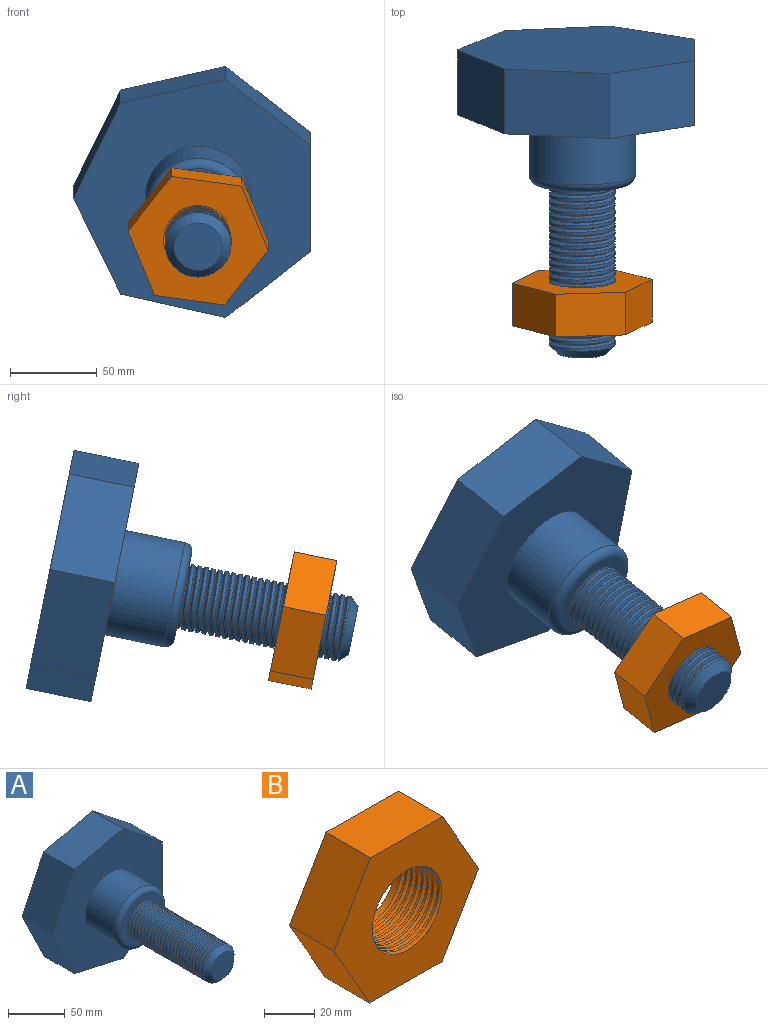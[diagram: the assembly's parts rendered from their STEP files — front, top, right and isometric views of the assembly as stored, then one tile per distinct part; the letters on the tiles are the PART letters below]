
ASSEMBLY  parts=2 mates=1
PART A: 20 faces, bbox 136.5x178.3x140 mm
  f0: plane 51.4x51.4mm, normal (0,-1,0), area 916.6mm2, adj f11,f12,f16,f17,f18
  f1: plane 48.65x38.8mm, normal (0.62,0,-0.78), area 2370.9mm2, adj f2,f7,f8,f9
  f2: plane 62.23x38.1mm, normal (1,0,0), area 2370.9mm2, adj f1,f3,f8,f9
  f3: plane 48.65x38.8mm, normal (0.62,0,0.78), area 2370.9mm2, adj f2,f4,f8,f9
  f4: plane 60.67x38.1mm, normal (-0.22,0,0.97), area 2370.9mm2, adj f3,f5,f8,f9
  f5: plane 56.07x38.1mm, normal (-0.9,0,0.43), area 2370.9mm2, adj f4,f6,f8,f9
  f6: plane 56.07x38.1mm, normal (-0.9,0,-0.43), area 2370.9mm2, adj f5,f7,f8,f9
  f7: plane 60.67x38.1mm, normal (-0.22,0,-0.97), area 2370.9mm2, adj f1,f6,f8,f9
  f8: plane 139.83x136.32mm, normal (0,-1,0), area 11125.9mm2, adj f1,f2,f3,f4,f5,f6,f7,f10
  f9: plane 139.83x136.32mm, normal (0,1,0), area 14072.4mm2, adj f1,f2,f3,f4,f5,f6,f7
  f10: cylinder r=30.62mm len=61.25mm, axis (0,1,0), area 6734.7mm2, adj f8,f11
  f11: torus R=25.62mm, axis (0,-1,0), area 1421.6mm2, adj f0,f10
  f12: cylinder r=18.94mm len=95mm, axis (0,1,0), area 4990.8mm2, adj f0,f14,f15,f16,f18,f19
  f13: plane 27.89x27.89mm, normal (0,-1,0), area 610.8mm2, adj f14
  f14: cone r=13.94mm half-angle=45deg, axis (0,1,0), area 722.4mm2, adj f12,f13,f15,f19
  f15: plane 1.86x1.84mm, normal (0.17,0,0.98), area 1.8mm2, adj f12,f14,f18,f19
  f16: plane 2.4x2.25mm, normal (0.98,0,-0.17), area 2.6mm2, adj f0,f12,f17,f18,f19
  f17: cylinder r=19.36mm len=33.03mm, axis (0,-1,0), area 39.5mm2, adj f0,f16,f18
  f18: bspline ~96.65x44.04mm, area 5813.6mm2, adj f0,f12,f15,f16,f17,f19
  f19: bspline ~96.65x44.04mm, area 5763.2mm2, adj f12,f14,f15,f16,f18
PART B: 20 faces, bbox 82.3x27.3x71.7 mm
  f0: plane 40.71x25mm, normal (-0.01,0,-1), area 1017.7mm2, adj f1,f5,f6,f7
  f1: plane 35.14x25mm, normal (0.86,0,-0.5), area 1017.7mm2, adj f0,f2,f6,f7
  f2: plane 35.37x25mm, normal (0.87,0,0.5), area 1017.7mm2, adj f1,f3,f6,f7
  f3: plane 40.71x25mm, normal (0.01,0,1), area 1017.7mm2, adj f2,f4,f6,f7
  f4: plane 35.14x25mm, normal (-0.86,0,0.5), area 1017.7mm2, adj f3,f5,f6,f7
  f5: plane 35.37x25mm, normal (-0.87,0,-0.5), area 1017.7mm2, adj f0,f4,f6,f7
  f6: plane 82.35x71.67mm, normal (0,-1,0), area 3103.6mm2, adj f0,f1,f2,f3,f4,f5,f16,f18
  f7: plane 81.42x70.74mm, normal (0,1,0), area 3160.8mm2, adj f0,f1,f2,f3,f4,f5,f8
  f8: cylinder r=19.09mm len=38.18mm, axis (0,1,0), area 297.9mm2, adj f7,f9,f17,f18,f19
  f9: cylinder r=19.09mm len=38.18mm, axis (0,1,0), area 140mm2, adj f8,f10,f18,f19
  f10: cylinder r=19.09mm len=38.18mm, axis (0,1,0), area 139.9mm2, adj f9,f11,f18,f19
  f11: cylinder r=19.09mm len=38.18mm, axis (0,1,0), area 139.8mm2, adj f10,f12,f18,f19
  f12: cylinder r=19.09mm len=38.18mm, axis (0,1,0), area 139.8mm2, adj f11,f13,f18,f19
  f13: cylinder r=19.09mm len=38.18mm, axis (0,1,0), area 139.9mm2, adj f12,f14,f18,f19
  f14: cylinder r=19.09mm len=38.18mm, axis (0,1,0), area 139.8mm2, adj f13,f15,f18,f19
  f15: cylinder r=19.09mm len=38.18mm, axis (0,1,0), area 139.8mm2, adj f14,f16,f18,f19
  f16: cylinder r=19.09mm len=27.68mm, axis (0,1,0), area 27.2mm2, adj f6,f15,f18
  f17: plane 1.83x1.32mm, normal (-0.87,0,0.5), area 1.4mm2, adj f8,f18,f19
  f18: bspline ~47.6x41.22mm, area 1673.7mm2, adj f6,f8,f9,f10,f11,f12,f13,f14
  f19: bspline ~47.6x41.22mm, area 1738.1mm2, adj f6,f8,f9,f10,f11,f12,f13,f14
PLACE A rot(axis=(0.02,-0.99,-0.1),154.4deg) t=(-37.17,-95.47,46.34)mm fixed
PLACE B rot(axis=(0.01,-1,-0.1),172.4deg) t=(-37.17,-210.06,23.21)mm
MATE cylindrical B.f8 <-> A.f12  axis (0,0.98,0.2) through (-37.17,-210.06,23.21)mm
